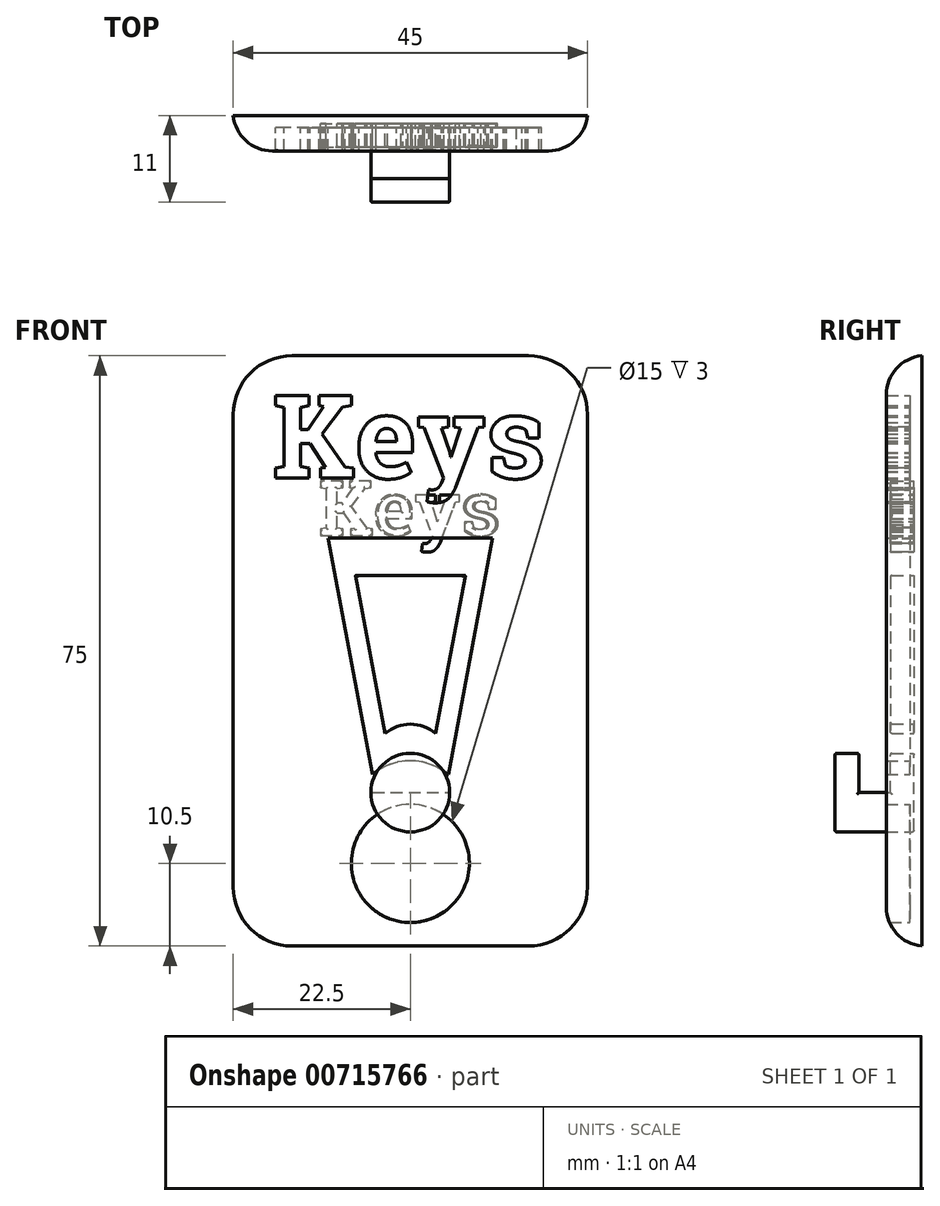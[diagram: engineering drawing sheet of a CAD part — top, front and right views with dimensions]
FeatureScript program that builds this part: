
annotation { "Feature Type Name" : "Feature", "Feature Type Description" : "" }
export const myFeature = defineFeature(function(context is Context, id is Id, definition is map)
    precondition{}
    {
        {
            var Q0;
            Q0=qCreatedBy(makeId("Front.planeOp"),FACE);
            var sketch = newSketch(context, id + "F0", { "sketchPlane" : qUnion([Q0])});
            skLineSegment(sketch, "E0.bottom", {"start": v(-10, 25) * mm, "end": v(10, 25) * mm});
            skLineSegment(sketch, "E0.top", {"start": v(-10, -25) * mm, "end": v(10, -25) * mm});
            skLineSegment(sketch, "E0.left", {"start": v(-15, 20) * mm, "end": v(-15, -20) * mm});
            skLineSegment(sketch, "E0.right", {"start": v(15, 20) * mm, "end": v(15, -20) * mm});
            skPoint(sketch, "E0.middle", {"position": v(0, 0) * mm});
            skCircle(sketch, "E1", {"center": v(0, -18) * mm, "radius": 5 * mm});
            skPoint(sketch, "E2", {"position": v(0, -25) * mm});
            skPoint(sketch, "E3.visualSharp", {"position": v(-15, 25) * mm});
            skArc(sketch, "E3.filletArc", {"start": v(-10, 25) * mm, "mid": v(-13.54, 23.54) * mm, "end": v(-15, 20) * mm});
            skPoint(sketch, "E4.visualSharp", {"position": v(15, 25) * mm});
            skArc(sketch, "E4.filletArc", {"start": v(15, 20) * mm, "mid": v(13.54, 23.54) * mm, "end": v(10, 25) * mm});
            skPoint(sketch, "E5.visualSharp", {"position": v(15, -25) * mm});
            skArc(sketch, "E5.filletArc", {"start": v(10, -25) * mm, "mid": v(13.54, -23.54) * mm, "end": v(15, -20) * mm});
            skPoint(sketch, "E6.visualSharp", {"position": v(-15, -25) * mm});
            skArc(sketch, "E6.filletArc", {"start": v(-15, -20) * mm, "mid": v(-13.54, -23.54) * mm, "end": v(-10, -25) * mm});
            skLineSegment(sketch, "E7", {"start": v(3.22, -10.48) * mm, "end": v(6.98, 9.55) * mm});
            skLineSegment(sketch, "E8", {"start": v(6.98, 9.55) * mm, "end": v(0, 9.55) * mm});
            skLineSegment(sketch, "E9", {"start": v(0, 25) * mm, "end": v(0, -25) * mm, "construction": true});
            skPoint(sketch, "E10", {"position": v(0, 9.55) * mm});
            skPoint(sketch, "E11", {"position": v(5.1, -0.47) * mm});
            skPoint(sketch, "E12.start.orphan", {"position": v(-6.98, 9.55) * mm});
            skLineSegment(sketch, "E13.MirrorCS", {"start": v(-6.98, 9.55) * mm, "end": v(0, 9.55) * mm});
            skLineSegment(sketch, "E14.MirrorCS", {"start": v(-3.22, -10.48) * mm, "end": v(-6.98, 9.55) * mm});
            skArc(sketch, "E15", {"start": v(3.22, -10.48) * mm, "mid": v(0, -9.3) * mm, "end": v(-3.22, -10.48) * mm});
            skText(sketch, "E16", { "text": "Keys", "fontName": "RobotoSlab-Bold.ttf"});
            skLineSegment(sketch, "E17", {"start": v(11.7, 18.17) * mm, "end": v(15, 18.17) * mm, "construction": true});
            skLineSegment(sketch, "E18", {"start": v(-11.7, 18.17) * mm, "end": v(-15, 18.17) * mm, "construction": true});
            skLineSegment(sketch, "E19", {"start": v(1.55, 25) * mm, "end": v(1.55, 21.7) * mm, "construction": true});
            skLineSegment(sketch, "E20", {"start": v(0, -9.3) * mm, "end": v(0, -13) * mm, "construction": true});
            const initialGuessF0  = {"E16": [-0.0117, 0.01463, 1, 0, 0.00707]};
            skSetInitialGuess(sketch, initialGuessF0);
            skSolve(sketch);
        }
        {
            var Q0;
            Q0 = qSketchRegion(id + "F0", true);
            var Q1;
            Q1=makeQuery(id+"F0.imprint","IMPRINT",FACE,{"disambiguationData":[TD([[makeQuery(id+"F0.imprint","IMPRINT",EDGE,{"derivedFrom":sQuery(id+"F0.wireOp",EDGE,"E0.bottom")}),-1.0]])]});
            var Q2;
            Q2=makeQuery(id+"F0.imprint","IMPRINT",FACE,{"disambiguationData":[TD([[makeQuery(id+"F0.imprint","IMPRINT",EDGE,{"derivedFrom":sQuery(id+"F0.wireOp",EDGE,"E1")}),1.0]])]});
            var Q3;
            Q3=makeQuery(id+"F0.imprint","IMPRINT",FACE,{"disambiguationData":[TD([[makeQuery(id+"F0.imprint","IMPRINT",EDGE,{"derivedFrom":sQuery(id+"F0.wireOp",EDGE,"E16.sketch_text.stroke-46")}),1.0]])]});
            var Q4;
            Q4=makeQuery(id+"F0.imprint","IMPRINT",FACE,{"disambiguationData":[TD([[makeQuery(id+"F0.imprint","IMPRINT",EDGE,{"derivedFrom":sQuery(id+"F0.wireOp",EDGE,"E16.sketch_text.stroke-29")}),-1.0]])]});
            var Q5;
            Q5=makeQuery(id+"F0.imprint","IMPRINT",FACE,{"disambiguationData":[TD([[makeQuery(id+"F0.imprint","IMPRINT",EDGE,{"derivedFrom":sQuery(id+"F0.wireOp",EDGE,"E16.sketch_text.stroke-53")}),-1.0]])]});
            var Q6;
            Q6=makeQuery(id+"F0.imprint","IMPRINT",FACE,{"disambiguationData":[TD([[makeQuery(id+"F0.imprint","IMPRINT",EDGE,{"derivedFrom":sQuery(id+"F0.wireOp",EDGE,"E16.sketch_text.stroke-79")}),-1.0]])]});
            var Q7;
            Q7=makeQuery(id+"F0.imprint","IMPRINT",FACE,{"disambiguationData":[TD([[makeQuery(id+"F0.imprint","IMPRINT",EDGE,{"derivedFrom":sQuery(id+"F0.wireOp",EDGE,"E16.sketch_text.stroke-0")}),-1.0]])]});
            var Q8;
            Q8=makeQuery(id+"F0.imprint","IMPRINT",FACE,{"disambiguationData":[TD([[makeQuery(id+"F0.imprint","IMPRINT",EDGE,{"derivedFrom":sQuery(id+"F0.wireOp",EDGE,"E7")}),1.0]])]});
            extrude(context, id + "F1", {"entities" : qUnion([Q0, Q1, Q2, Q3, Q4, Q5, Q6, Q7, Q8]), "depth" : 1 * mm, "offsetDistance" : 25 * mm});
        }
        {
            var Q0;
            Q0=makeQuery(id+"F0.imprint","IMPRINT",FACE,{"disambiguationData":[TD([[makeQuery(id+"F0.imprint","IMPRINT",EDGE,{"derivedFrom":sQuery(id+"F0.wireOp",EDGE,"E0.bottom")}),-1.0]])]});
            var Q1;
            Q1=makeQuery(id+"F0.imprint","IMPRINT",FACE,{"disambiguationData":[TD([[makeQuery(id+"F0.imprint","IMPRINT",EDGE,{"derivedFrom":sQuery(id+"F0.wireOp",EDGE,"E16.sketch_text.stroke-46")}),1.0]])]});
            extrude(context, id + "F2", {"entities" : qUnion([Q0, Q1]), "operationType" : NewBodyOperationType.ADD, "depth" : 3 * mm, "offsetDistance" : 25 * mm});
        }
        {
            var Q0;
            Q0=makeQuery(id+"F2.boolean.opBoolean","SPLIT",FACE,{"disambiguationData":[TD([makeQuery(id+"F2.opExtrude","SWEPT_FACE",FACE,{"disambiguationData":[OSD([sQuery(id+"F0.wireOp",EDGE,"E7")])]})])],"derivedFrom":makeQuery(id+"F1.opExtrude","CAP_FACE",FACE,{"disambiguationData":[OSD([sQuery(id+"F0.wireOp",EDGE,"E0.bottom"),sQuery(id+"F0.wireOp",EDGE,"E0.top"),sQuery(id+"F0.wireOp",EDGE,"E0.left"),sQuery(id+"F0.wireOp",EDGE,"E0.right"),sQuery(id+"F0.wireOp",EDGE,"E3.filletArc"),sQuery(id+"F0.wireOp",EDGE,"E4.filletArc"),sQuery(id+"F0.wireOp",EDGE,"E5.filletArc"),sQuery(id+"F0.wireOp",EDGE,"E6.filletArc")])],"isStart":false})});
            var Q1;
            Q1=makeQuery(id+"F2.boolean.opBoolean","SPLIT",FACE,{"disambiguationData":[TD([makeQuery(id+"F2.opExtrude","SWEPT_FACE",FACE,{"disambiguationData":[OSD([sQuery(id+"F0.wireOp",EDGE,"E16.sketch_text.stroke-0")])]})])],"derivedFrom":makeQuery(id+"F1.opExtrude","CAP_FACE",FACE,{"disambiguationData":[OSD([sQuery(id+"F0.wireOp",EDGE,"E0.bottom"),sQuery(id+"F0.wireOp",EDGE,"E0.top"),sQuery(id+"F0.wireOp",EDGE,"E0.left"),sQuery(id+"F0.wireOp",EDGE,"E0.right"),sQuery(id+"F0.wireOp",EDGE,"E3.filletArc"),sQuery(id+"F0.wireOp",EDGE,"E4.filletArc"),sQuery(id+"F0.wireOp",EDGE,"E5.filletArc"),sQuery(id+"F0.wireOp",EDGE,"E6.filletArc")])],"isStart":false})});
            var Q2;
            Q2=makeQuery(id+"F2.boolean.opBoolean","SPLIT",FACE,{"disambiguationData":[TD([makeQuery(id+"F2.opExtrude","SWEPT_FACE",FACE,{"disambiguationData":[OSD([sQuery(id+"F0.wireOp",EDGE,"E16.sketch_text.stroke-29")])]})])],"derivedFrom":makeQuery(id+"F1.opExtrude","CAP_FACE",FACE,{"disambiguationData":[OSD([sQuery(id+"F0.wireOp",EDGE,"E0.bottom"),sQuery(id+"F0.wireOp",EDGE,"E0.top"),sQuery(id+"F0.wireOp",EDGE,"E0.left"),sQuery(id+"F0.wireOp",EDGE,"E0.right"),sQuery(id+"F0.wireOp",EDGE,"E3.filletArc"),sQuery(id+"F0.wireOp",EDGE,"E4.filletArc"),sQuery(id+"F0.wireOp",EDGE,"E5.filletArc"),sQuery(id+"F0.wireOp",EDGE,"E6.filletArc")])],"isStart":false})});
            var Q3;
            Q3=makeQuery(id+"F2.boolean.opBoolean","SPLIT",FACE,{"disambiguationData":[TD([makeQuery(id+"F2.opExtrude","SWEPT_FACE",FACE,{"disambiguationData":[OSD([sQuery(id+"F0.wireOp",EDGE,"E16.sketch_text.stroke-53")])]})])],"derivedFrom":makeQuery(id+"F1.opExtrude","CAP_FACE",FACE,{"disambiguationData":[OSD([sQuery(id+"F0.wireOp",EDGE,"E0.bottom"),sQuery(id+"F0.wireOp",EDGE,"E0.top"),sQuery(id+"F0.wireOp",EDGE,"E0.left"),sQuery(id+"F0.wireOp",EDGE,"E0.right"),sQuery(id+"F0.wireOp",EDGE,"E3.filletArc"),sQuery(id+"F0.wireOp",EDGE,"E4.filletArc"),sQuery(id+"F0.wireOp",EDGE,"E5.filletArc"),sQuery(id+"F0.wireOp",EDGE,"E6.filletArc")])],"isStart":false})});
            var Q4;
            Q4=makeQuery(id+"F2.boolean.opBoolean","SPLIT",FACE,{"disambiguationData":[TD([makeQuery(id+"F2.opExtrude","SWEPT_FACE",FACE,{"disambiguationData":[OSD([sQuery(id+"F0.wireOp",EDGE,"E16.sketch_text.stroke-79")])]})])],"derivedFrom":makeQuery(id+"F1.opExtrude","CAP_FACE",FACE,{"disambiguationData":[OSD([sQuery(id+"F0.wireOp",EDGE,"E0.bottom"),sQuery(id+"F0.wireOp",EDGE,"E0.top"),sQuery(id+"F0.wireOp",EDGE,"E0.left"),sQuery(id+"F0.wireOp",EDGE,"E0.right"),sQuery(id+"F0.wireOp",EDGE,"E3.filletArc"),sQuery(id+"F0.wireOp",EDGE,"E4.filletArc"),sQuery(id+"F0.wireOp",EDGE,"E5.filletArc"),sQuery(id+"F0.wireOp",EDGE,"E6.filletArc")])],"isStart":false})});
            extrude(context, id + "F3", {"entities" : qUnion([Q0, Q1, Q2, Q3, Q4]), "depth" : 3 * mm, "offsetDistance" : 25 * mm});
        }
        {
            var Q0;
            Q0=makeQuery(id+"F2.boolean.opBoolean","SPLIT",FACE,{"disambiguationData":[TD([makeQuery(id+"F2.opExtrude","SWEPT_FACE",FACE,{"disambiguationData":[OSD([sQuery(id+"F0.wireOp",EDGE,"E1")])]})])],"derivedFrom":makeQuery(id+"F1.opExtrude","CAP_FACE",FACE,{"disambiguationData":[OSD([sQuery(id+"F0.wireOp",EDGE,"E0.bottom"),sQuery(id+"F0.wireOp",EDGE,"E0.top"),sQuery(id+"F0.wireOp",EDGE,"E0.left"),sQuery(id+"F0.wireOp",EDGE,"E0.right"),sQuery(id+"F0.wireOp",EDGE,"E3.filletArc"),sQuery(id+"F0.wireOp",EDGE,"E4.filletArc"),sQuery(id+"F0.wireOp",EDGE,"E5.filletArc"),sQuery(id+"F0.wireOp",EDGE,"E6.filletArc")])],"isStart":false})});
            extrude(context, id + "F4", {"entities" : qUnion([Q0]), "depth" : 10 * mm, "offsetDistance" : 25 * mm});
        }
        {
            var Q0;
            Q0=qCreatedBy(makeId("Top.planeOp"),FACE);
            var sketch = newSketch(context, id + "F5", { "sketchPlane" : qUnion([Q0])});
            skLineSegment(sketch, "E21", {"start": v(-5, -11) * mm, "end": v(-5, -3) * mm});
            skLineSegment(sketch, "E22", {"start": v(5, -3) * mm, "end": v(5, -11) * mm});
            skLineSegment(sketch, "E23", {"start": v(-5, -8) * mm, "end": v(5, -8) * mm});
            skLineSegment(sketch, "E24", {"start": v(-5, -4) * mm, "end": v(5, -4) * mm});
            skSolve(sketch);
        }
        {
            var Q0;
            {var subQ0=sQuery(id+"F5.wireOp",EDGE,"E23");Q0=makeQuery(id+"F5.imprint","IMPRINT",FACE,{"disambiguationData":[TD([[makeQuery(id+"F5.imprint","IMPRINT",EDGE,{"derivedFrom":subQ0}),1.0]])]});}
            extrude(context, id + "F6", {"entities" : qUnion([Q0]), "operationType" : NewBodyOperationType.REMOVE, "oppositeDirection" : true, "depth" : 18 * mm, "offsetDistance" : 25 * mm});
        }
        {
            var Q0;
            Q0=makeQuery(id+"F1.opExtrude","SWEPT_BODY",BODY,{"disambiguationData":[OSD([sQuery(id+"F0.wireOp",EDGE,"E0.bottom"),sQuery(id+"F0.wireOp",EDGE,"E0.top"),sQuery(id+"F0.wireOp",EDGE,"E0.left"),sQuery(id+"F0.wireOp",EDGE,"E0.right"),sQuery(id+"F0.wireOp",EDGE,"E3.filletArc"),sQuery(id+"F0.wireOp",EDGE,"E4.filletArc"),sQuery(id+"F0.wireOp",EDGE,"E5.filletArc"),sQuery(id+"F0.wireOp",EDGE,"E6.filletArc")])]});
            var Q1;
            Q1=qCreatedBy(makeId("Origin.pointOp"),VERTEX);
            transform(context, id + "F7", {"entities" : qUnion([Q0]), "transformType" : TransformType.SCALE_UNIFORMLY, "scale" : 1.5, "scalePoint" : qUnion([Q1]), "makeCopy" : false});
        }
        {
            var Q0;
            Q0=makeQuery(id+"F2.opExtrude","CAP_EDGE",EDGE,{"disambiguationData":[OSD([sQuery(id+"F0.wireOp",EDGE,"E0.left")])],"isStart":false});
            fillet(context, id + "F8", {"entities" : qUnion([Q0]), "radius" : 5 * mm, "tangentPropagation" : true, "allowEdgeOverflow" : false});
        }
        {
            var Q0;
            {var subQ0=sQuery(id+"F0.wireOp",EDGE,"E6.filletArc");var subQ1=sQuery(id+"F0.wireOp",EDGE,"E5.filletArc");var subQ2=sQuery(id+"F0.wireOp",EDGE,"E4.filletArc");var subQ3=sQuery(id+"F0.wireOp",EDGE,"E3.filletArc");var subQ4=sQuery(id+"F0.wireOp",EDGE,"E0.right");var subQ5=sQuery(id+"F0.wireOp",EDGE,"E0.left");var subQ6=sQuery(id+"F0.wireOp",EDGE,"E0.top");var subQ7=sQuery(id+"F0.wireOp",EDGE,"E0.bottom");Q0=makeQuery(id+"F3.opExtrude","CAP_FACE",FACE,{"disambiguationData":[OSD([subQ7,subQ6,subQ5,subQ4,subQ3,subQ2,subQ1,subQ0]),TDD([makeQuery(id+"F2.boolean.opBoolean","SPLIT",FACE,{"disambiguationData":[TD([makeQuery(id+"F2.opExtrude","SWEPT_FACE",FACE,{"disambiguationData":[OSD([sQuery(id+"F0.wireOp",EDGE,"E7")])]})])],"derivedFrom":makeQuery(id+"F1.opExtrude","CAP_FACE",FACE,{"disambiguationData":[OSD([subQ7,subQ6,subQ5,subQ4,subQ3,subQ2,subQ1,subQ0])],"isStart":false})})])],"isStart":false});}
            var Q1;
            {var subQ0=sQuery(id+"F0.wireOp",EDGE,"E6.filletArc");var subQ1=sQuery(id+"F0.wireOp",EDGE,"E5.filletArc");var subQ2=sQuery(id+"F0.wireOp",EDGE,"E4.filletArc");var subQ3=sQuery(id+"F0.wireOp",EDGE,"E3.filletArc");var subQ4=sQuery(id+"F0.wireOp",EDGE,"E0.right");var subQ5=sQuery(id+"F0.wireOp",EDGE,"E0.left");var subQ6=sQuery(id+"F0.wireOp",EDGE,"E0.top");var subQ7=sQuery(id+"F0.wireOp",EDGE,"E0.bottom");Q1=makeQuery(id+"F3.opExtrude","CAP_FACE",FACE,{"disambiguationData":[OSD([subQ7,subQ6,subQ5,subQ4,subQ3,subQ2,subQ1,subQ0]),TDD([makeQuery(id+"F2.boolean.opBoolean","SPLIT",FACE,{"disambiguationData":[TD([makeQuery(id+"F2.opExtrude","SWEPT_FACE",FACE,{"disambiguationData":[OSD([sQuery(id+"F0.wireOp",EDGE,"E16.sketch_text.stroke-53")])]})])],"derivedFrom":makeQuery(id+"F1.opExtrude","CAP_FACE",FACE,{"disambiguationData":[OSD([subQ7,subQ6,subQ5,subQ4,subQ3,subQ2,subQ1,subQ0])],"isStart":false})})])],"isStart":false});}
            var Q2;
            {var subQ0=sQuery(id+"F0.wireOp",EDGE,"E6.filletArc");var subQ1=sQuery(id+"F0.wireOp",EDGE,"E5.filletArc");var subQ2=sQuery(id+"F0.wireOp",EDGE,"E4.filletArc");var subQ3=sQuery(id+"F0.wireOp",EDGE,"E3.filletArc");var subQ4=sQuery(id+"F0.wireOp",EDGE,"E0.right");var subQ5=sQuery(id+"F0.wireOp",EDGE,"E0.left");var subQ6=sQuery(id+"F0.wireOp",EDGE,"E0.top");var subQ7=sQuery(id+"F0.wireOp",EDGE,"E0.bottom");Q2=makeQuery(id+"F3.opExtrude","CAP_FACE",FACE,{"disambiguationData":[OSD([subQ7,subQ6,subQ5,subQ4,subQ3,subQ2,subQ1,subQ0]),TDD([makeQuery(id+"F2.boolean.opBoolean","SPLIT",FACE,{"disambiguationData":[TD([makeQuery(id+"F2.opExtrude","SWEPT_FACE",FACE,{"disambiguationData":[OSD([sQuery(id+"F0.wireOp",EDGE,"E16.sketch_text.stroke-79")])]})])],"derivedFrom":makeQuery(id+"F1.opExtrude","CAP_FACE",FACE,{"disambiguationData":[OSD([subQ7,subQ6,subQ5,subQ4,subQ3,subQ2,subQ1,subQ0])],"isStart":false})})])],"isStart":false});}
            var Q3;
            {var subQ0=sQuery(id+"F0.wireOp",EDGE,"E6.filletArc");var subQ1=sQuery(id+"F0.wireOp",EDGE,"E5.filletArc");var subQ2=sQuery(id+"F0.wireOp",EDGE,"E4.filletArc");var subQ3=sQuery(id+"F0.wireOp",EDGE,"E3.filletArc");var subQ4=sQuery(id+"F0.wireOp",EDGE,"E0.right");var subQ5=sQuery(id+"F0.wireOp",EDGE,"E0.left");var subQ6=sQuery(id+"F0.wireOp",EDGE,"E0.top");var subQ7=sQuery(id+"F0.wireOp",EDGE,"E0.bottom");Q3=makeQuery(id+"F3.opExtrude","CAP_FACE",FACE,{"disambiguationData":[OSD([subQ7,subQ6,subQ5,subQ4,subQ3,subQ2,subQ1,subQ0]),TDD([makeQuery(id+"F2.boolean.opBoolean","SPLIT",FACE,{"disambiguationData":[TD([makeQuery(id+"F2.opExtrude","SWEPT_FACE",FACE,{"disambiguationData":[OSD([sQuery(id+"F0.wireOp",EDGE,"E16.sketch_text.stroke-29")])]})])],"derivedFrom":makeQuery(id+"F1.opExtrude","CAP_FACE",FACE,{"disambiguationData":[OSD([subQ7,subQ6,subQ5,subQ4,subQ3,subQ2,subQ1,subQ0])],"isStart":false})})])],"isStart":false});}
            var Q4;
            {var subQ0=sQuery(id+"F0.wireOp",EDGE,"E6.filletArc");var subQ1=sQuery(id+"F0.wireOp",EDGE,"E5.filletArc");var subQ2=sQuery(id+"F0.wireOp",EDGE,"E4.filletArc");var subQ3=sQuery(id+"F0.wireOp",EDGE,"E3.filletArc");var subQ4=sQuery(id+"F0.wireOp",EDGE,"E0.right");var subQ5=sQuery(id+"F0.wireOp",EDGE,"E0.left");var subQ6=sQuery(id+"F0.wireOp",EDGE,"E0.top");var subQ7=sQuery(id+"F0.wireOp",EDGE,"E0.bottom");Q4=makeQuery(id+"F3.opExtrude","CAP_FACE",FACE,{"disambiguationData":[OSD([subQ7,subQ6,subQ5,subQ4,subQ3,subQ2,subQ1,subQ0]),TDD([makeQuery(id+"F2.boolean.opBoolean","SPLIT",FACE,{"disambiguationData":[TD([makeQuery(id+"F2.opExtrude","SWEPT_FACE",FACE,{"disambiguationData":[OSD([sQuery(id+"F0.wireOp",EDGE,"E16.sketch_text.stroke-0")])]})])],"derivedFrom":makeQuery(id+"F1.opExtrude","CAP_FACE",FACE,{"disambiguationData":[OSD([subQ7,subQ6,subQ5,subQ4,subQ3,subQ2,subQ1,subQ0])],"isStart":false})})])],"isStart":false});}
            var Q5;
            Q5=makeQuery(id+"F4.opExtrude","CAP_FACE",FACE,{"disambiguationData":[OSD([sQuery(id+"F0.wireOp",EDGE,"E0.bottom"),sQuery(id+"F0.wireOp",EDGE,"E0.top"),sQuery(id+"F0.wireOp",EDGE,"E0.left"),sQuery(id+"F0.wireOp",EDGE,"E0.right"),sQuery(id+"F0.wireOp",EDGE,"E3.filletArc"),sQuery(id+"F0.wireOp",EDGE,"E4.filletArc"),sQuery(id+"F0.wireOp",EDGE,"E5.filletArc"),sQuery(id+"F0.wireOp",EDGE,"E6.filletArc")])],"isStart":false});
            var Q6;
            Q6=makeQuery(id+"F4.opExtrude","SWEPT_FACE",FACE,{"disambiguationData":[OSD([sQuery(id+"F0.wireOp",EDGE,"E0.bottom"),sQuery(id+"F0.wireOp",EDGE,"E0.top"),sQuery(id+"F0.wireOp",EDGE,"E0.left"),sQuery(id+"F0.wireOp",EDGE,"E0.right"),sQuery(id+"F0.wireOp",EDGE,"E1"),sQuery(id+"F0.wireOp",EDGE,"E3.filletArc"),sQuery(id+"F0.wireOp",EDGE,"E4.filletArc"),sQuery(id+"F0.wireOp",EDGE,"E5.filletArc"),sQuery(id+"F0.wireOp",EDGE,"E6.filletArc")])]});
            fillet(context, id + "F9", {"entities" : qUnion([Q0, Q1, Q2, Q3, Q4, Q5, Q6]), "radius" : 0.2 * mm, "tangentPropagation" : true, "allowEdgeOverflow" : false});
        }
    });
